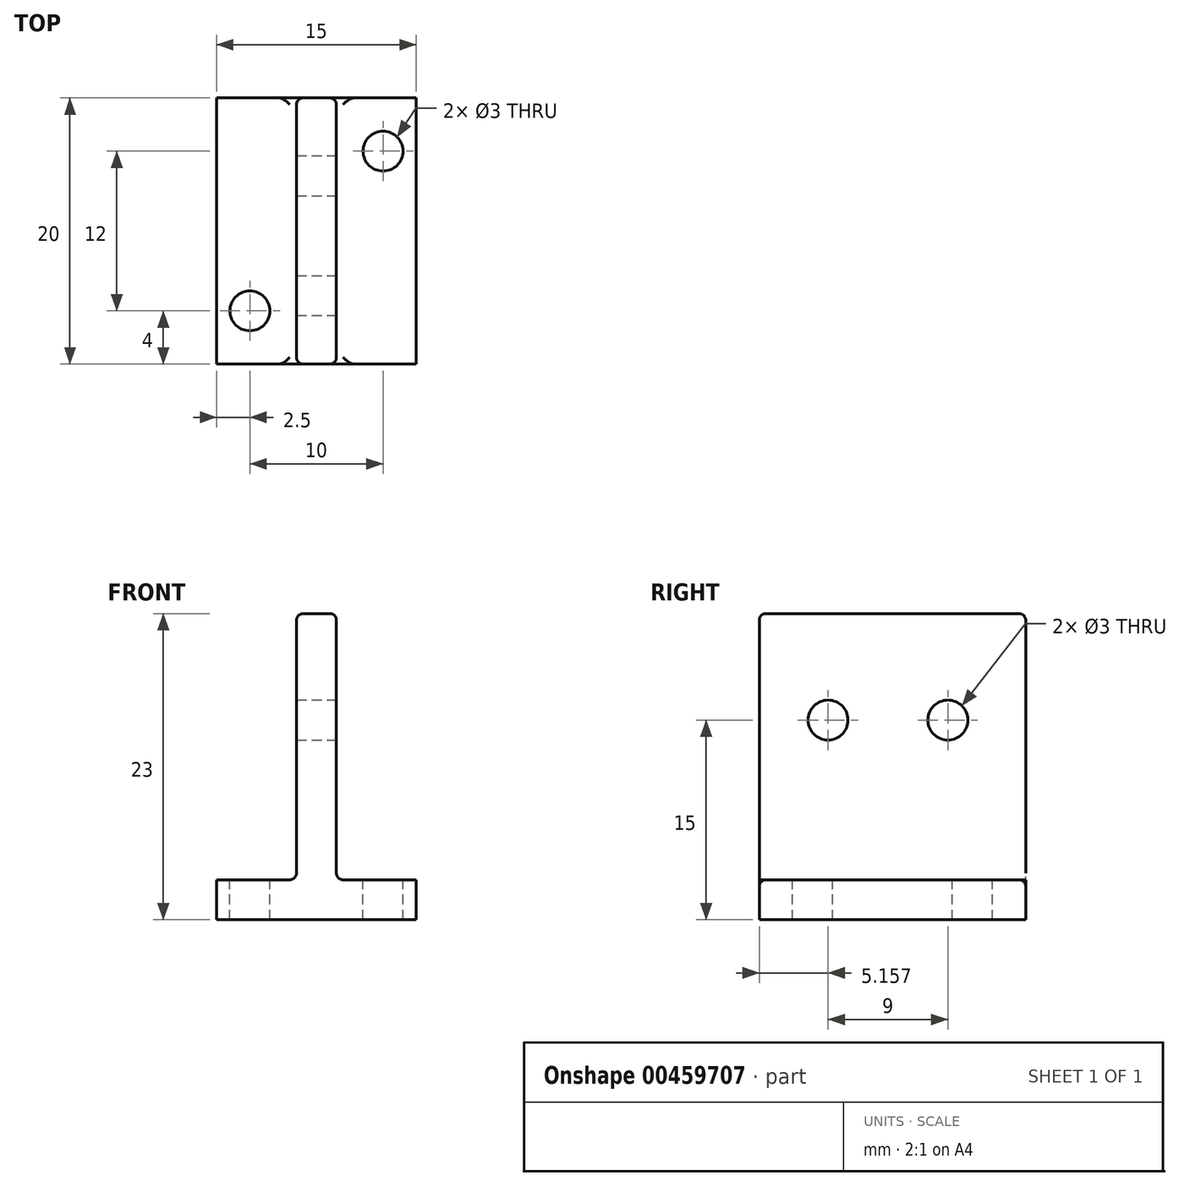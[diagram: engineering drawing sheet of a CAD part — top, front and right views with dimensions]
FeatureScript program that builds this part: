
annotation { "Feature Type Name" : "Feature", "Feature Type Description" : "" }
export const myFeature = defineFeature(function(context is Context, id is Id, definition is map)
    precondition{}
    {
        {
            var Q0;
            Q0=qCreatedBy(makeId("Front.planeOp"),FACE);
            var sketch = newSketch(context, id + "F0", { "sketchPlane" : qUnion([Q0])});
            skLineSegment(sketch, "E0.bottom", {"start": v(1.5, 10) * mm, "end": v(-1.5, 10) * mm});
            skLineSegment(sketch, "E0.top", {"start": v(1.5, -10) * mm, "end": v(-1.5, -10) * mm});
            skLineSegment(sketch, "E0.left", {"start": v(1.5, 10) * mm, "end": v(1.5, -10) * mm});
            skLineSegment(sketch, "E0.right", {"start": v(-1.5, 10) * mm, "end": v(-1.5, -10) * mm});
            skPoint(sketch, "E0.middle", {"position": v(0, 0) * mm});
            skPoint(sketch, "E1.middle", {"position": v(-1.5, -10) * mm});
            skLineSegment(sketch, "E2", {"start": v(-1.5, -10) * mm, "end": v(-7.5, -10) * mm});
            skLineSegment(sketch, "E3", {"start": v(-7.5, -10) * mm, "end": v(-7.5, -13) * mm});
            skLineSegment(sketch, "E4", {"start": v(-7.5, -13) * mm, "end": v(7.5, -13) * mm});
            skLineSegment(sketch, "E5", {"start": v(7.5, -13) * mm, "end": v(7.5, -10) * mm});
            skLineSegment(sketch, "E6", {"start": v(7.5, -10) * mm, "end": v(1.5, -10) * mm});
            skSolve(sketch);
        }
        {
            var Q0;
            Q0=makeQuery(id+"F0.imprint","IMPRINT",FACE,{"disambiguationData":[TD([[makeQuery(id+"F0.imprint","IMPRINT",EDGE,{"derivedFrom":sQuery(id+"F0.wireOp",EDGE,"E0.bottom")}),1.0]])]});
            var Q1;
            Q1=makeQuery(id+"F0.imprint","IMPRINT",FACE,{"disambiguationData":[TD([[makeQuery(id+"F0.imprint","IMPRINT",EDGE,{"derivedFrom":sQuery(id+"F0.wireOp",EDGE,"E0.top")}),1.0]])]});
            extrude(context, id + "F1", {"entities" : qUnion([Q0, Q1]), "depth" : 20 * mm});
        }
        {
            var Q0;
            Q0=makeQuery(id+"F1.opExtrude","SWEPT_FACE",FACE,{"disambiguationData":[OSD([sQuery(id+"F0.wireOp",EDGE,"E0.left")])]});
            var sketch = newSketch(context, id + "F2", { "sketchPlane" : qUnion([Q0])});
            skCircle(sketch, "E7", {"center": v(-14.84, 2) * mm, "radius": 1.5 * mm});
            skCircle(sketch, "E8", {"center": v(-5.84, 2) * mm, "radius": 1.5 * mm});
            skSolve(sketch);
        }
        {
            var Q0;
            Q0=makeQuery(id+"F2.imprint","IMPRINT",FACE,{"disambiguationData":[TD([[makeQuery(id+"F2.imprint","IMPRINT",EDGE,{"derivedFrom":sQuery(id+"F2.wireOp",EDGE,"E7")}),1.0]])]});
            var Q1;
            Q1=makeQuery(id+"F2.imprint","IMPRINT",FACE,{"disambiguationData":[TD([[makeQuery(id+"F2.imprint","IMPRINT",EDGE,{"derivedFrom":sQuery(id+"F2.wireOp",EDGE,"E8")}),1.0]])]});
            extrude(context, id + "F3", {"entities" : qUnion([Q0, Q1]), "operationType" : NewBodyOperationType.REMOVE, "endBound" : BoundingType.THROUGH_ALL, "oppositeDirection" : true, "depth" : 25 * mm});
        }
        {
            var Q0;
            Q0=makeQuery(id+"F1.opExtrude","SWEPT_FACE",FACE,{"disambiguationData":[OSD([sQuery(id+"F0.wireOp",EDGE,"E6")])]});
            var sketch = newSketch(context, id + "F4", { "sketchPlane" : qUnion([Q0])});
            skCircle(sketch, "E9", {"center": v(5, -4) * mm, "radius": 1.5 * mm});
            skSolve(sketch);
        }
        {
            var Q0;
            Q0=makeQuery(id+"F4.imprint","IMPRINT",FACE,{"disambiguationData":[TD([[makeQuery(id+"F4.imprint","IMPRINT",EDGE,{"derivedFrom":sQuery(id+"F4.wireOp",EDGE,"E9")}),1.0]])]});
            extrude(context, id + "F5", {"entities" : qUnion([Q0]), "operationType" : NewBodyOperationType.REMOVE, "endBound" : BoundingType.THROUGH_ALL, "oppositeDirection" : true, "depth" : 25 * mm});
        }
        {
            var Q0;
            Q0=makeQuery(id+"F1.opExtrude","SWEPT_FACE",FACE,{"disambiguationData":[OSD([sQuery(id+"F0.wireOp",EDGE,"E2")])]});
            var sketch = newSketch(context, id + "F6", { "sketchPlane" : qUnion([Q0])});
            skCircle(sketch, "E10", {"center": v(-5, -16) * mm, "radius": 1.5 * mm});
            skSolve(sketch);
        }
        {
            var Q0;
            Q0=qSketchRegion(id+"F6",true);
            extrude(context, id + "F7", {"entities" : qUnion([Q0]), "operationType" : NewBodyOperationType.REMOVE, "oppositeDirection" : true, "depth" : 25 * mm});
        }
        {
            var Q0;
            Q0=makeQuery(id+"F1.opExtrude","SWEPT_EDGE",EDGE,{"disambiguationData":[OSD([sQuery(id+"F0.wireOp",EDGE,"E0.top"),sQuery(id+"F0.wireOp",EDGE,"E0.left"),sQuery(id+"F0.wireOp",EDGE,"E6")])]});
            var Q1;
            Q1=makeQuery(id+"F1.opExtrude","SWEPT_EDGE",EDGE,{"disambiguationData":[OSD([sQuery(id+"F0.wireOp",EDGE,"E0.top"),sQuery(id+"F0.wireOp",EDGE,"E0.right"),sQuery(id+"F0.wireOp",EDGE,"E2")])]});
            var Q2;
            Q2=makeQuery(id+"F1.opExtrude","SWEPT_EDGE",EDGE,{"disambiguationData":[OSD([sQuery(id+"F0.wireOp",EDGE,"E0.bottom"),sQuery(id+"F0.wireOp",EDGE,"E0.right")])]});
            var Q3;
            Q3=makeQuery(id+"F1.opExtrude","CAP_EDGE",EDGE,{"disambiguationData":[OSD([sQuery(id+"F0.wireOp",EDGE,"E0.left")])],"isStart":false});
            var Q4;
            Q4=makeQuery(id+"F1.opExtrude","CAP_EDGE",EDGE,{"disambiguationData":[OSD([sQuery(id+"F0.wireOp",EDGE,"E0.right")])],"isStart":false});
            var Q5;
            Q5=makeQuery(id+"F1.opExtrude","SWEPT_EDGE",EDGE,{"disambiguationData":[OSD([sQuery(id+"F0.wireOp",EDGE,"E0.bottom"),sQuery(id+"F0.wireOp",EDGE,"E0.left")])]});
            var Q6;
            Q6=makeQuery(id+"F1.opExtrude","CAP_EDGE",EDGE,{"disambiguationData":[OSD([sQuery(id+"F0.wireOp",EDGE,"E0.right")])],"isStart":true});
            var Q7;
            Q7=makeQuery(id+"F1.opExtrude","CAP_EDGE",EDGE,{"disambiguationData":[OSD([sQuery(id+"F0.wireOp",EDGE,"E0.left")])],"isStart":true});
            var Q8;
            Q8=makeQuery(id+"F1.opExtrude","CAP_EDGE",EDGE,{"disambiguationData":[OSD([sQuery(id+"F0.wireOp",EDGE,"E0.bottom")])],"isStart":false});
            var Q9;
            Q9=makeQuery(id+"F1.opExtrude","CAP_EDGE",EDGE,{"disambiguationData":[OSD([sQuery(id+"F0.wireOp",EDGE,"E0.bottom")])],"isStart":true});
            fillet(context, id + "F8", {"entities" : qUnion([Q0, Q1, Q2, Q3, Q4, Q5, Q6, Q7, Q8, Q9]), "radius" : .5 * mm, "tangentPropagation" : true, "allowEdgeOverflow" : false});
        }
    });
